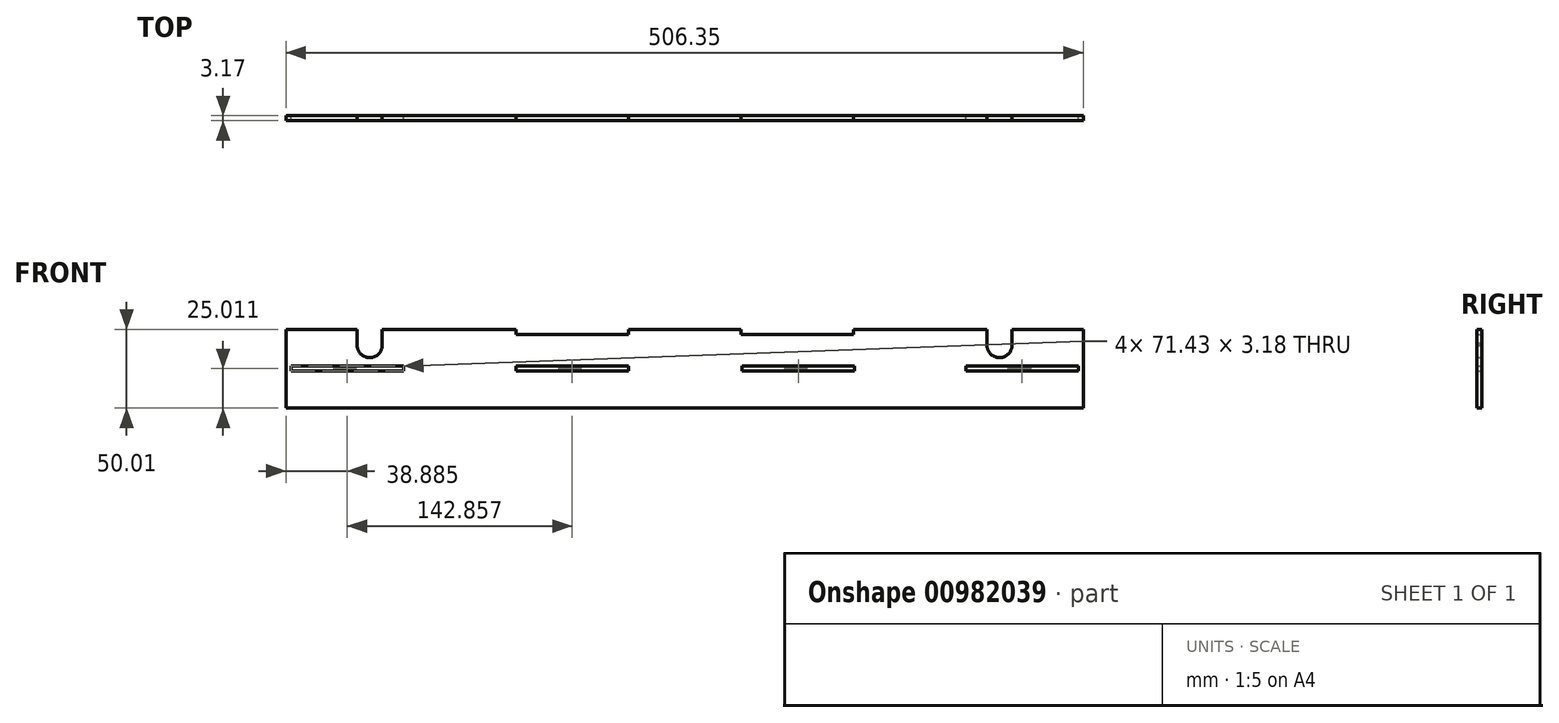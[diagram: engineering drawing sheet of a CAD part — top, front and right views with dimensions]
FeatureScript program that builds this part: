
annotation { "Feature Type Name" : "Feature", "Feature Type Description" : "" }
export const myFeature = defineFeature(function(context is Context, id is Id, definition is map)
    precondition{}
    {
        {
            var Q0;
            Q0=qCreatedBy(makeId("Front.planeOp"),FACE);
            var sketch = newSketch(context, id + "F0", { "sketchPlane" : qUnion([Q0])});
            skLineSegment(sketch, "E0.left", {"start": v(161.22, -50.9) * mm, "end": v(161.22, -0.9) * mm});
            skLineSegment(sketch, "E0.right", {"start": v(-338.78, -50.9) * mm, "end": v(-338.78, -0.9) * mm});
            skCircle(sketch, "E1", {"center": v(-288.78, -10.9) * mm, "radius": 8 * mm});
            skLineSegment(sketch, "E2", {"start": v(-88.78, -0.9) * mm, "end": v(-88.78, -50.9) * mm, "construction": true});
            skLineSegment(sketch, "E3.left", {"start": v(-338.78, -27.5) * mm, "end": v(-338.78, -24.32) * mm});
            skLineSegment(sketch, "E4", {"start": v(-338.78, -50.9) * mm, "end": v(161.22, -50.9) * mm});
            skCircle(sketch, "E5.MirrorC", {"center": v(111.22, -10.9) * mm, "radius": 8 * mm});
            skLineSegment(sketch, "E6.top", {"start": v(-296.77, -0.9) * mm, "end": v(-280.87, -0.9) * mm});
            skLineSegment(sketch, "E6.left", {"start": v(-296.77, -11.3) * mm, "end": v(-296.77, -0.9) * mm});
            skLineSegment(sketch, "E6.right", {"start": v(-280.87, -11.3) * mm, "end": v(-280.87, -0.9) * mm});
            skLineSegment(sketch, "E7", {"start": v(-296.77, -11.3) * mm, "end": v(-280.87, -11.3) * mm});
            skLineSegment(sketch, "E8.bottom", {"start": v(103.22, -11.1) * mm, "end": v(119.26, -11.1) * mm});
            skLineSegment(sketch, "E8.top", {"start": v(103.22, -0.9) * mm, "end": v(119.26, -0.9) * mm});
            skLineSegment(sketch, "E8.left", {"start": v(103.22, -11.1) * mm, "end": v(103.22, -0.9) * mm});
            skLineSegment(sketch, "E8.right", {"start": v(119.26, -11.1) * mm, "end": v(119.26, -0.9) * mm});
            skLineSegment(sketch, "E9.bottom", {"start": v(161.22, -24.32) * mm, "end": v(-338.78, -24.32) * mm, "construction": true});
            skLineSegment(sketch, "E10.top", {"start": v(-338.78, -27.5) * mm, "end": v(-267.35, -27.5) * mm});
            skLineSegment(sketch, "E10.left", {"start": v(-338.78, -24.32) * mm, "end": v(-338.78, -27.5) * mm});
            skLineSegment(sketch, "E10.right", {"start": v(-267.35, -24.32) * mm, "end": v(-267.35, -27.5) * mm});
            skLineSegment(sketch, "E11.1.0.0", {"start": v(-195.92, -27.5) * mm, "end": v(-124.5, -27.5) * mm});
            skLineSegment(sketch, "E11.1.0.2", {"start": v(-195.92, -24.32) * mm, "end": v(-195.92, -27.5) * mm});
            skLineSegment(sketch, "E11.1.0.3", {"start": v(-124.5, -24.32) * mm, "end": v(-124.5, -27.5) * mm});
            skLineSegment(sketch, "E11.1.0.4", {"start": v(-124.5, -24.32) * mm, "end": v(-124.5, -27.5) * mm});
            skLineSegment(sketch, "E11.2.0.0", {"start": v(-52.25, -27.5) * mm, "end": v(19.18, -27.5) * mm});
            skLineSegment(sketch, "E11.2.0.2", {"start": v(-52.25, -24.32) * mm, "end": v(-52.25, -27.5) * mm});
            skLineSegment(sketch, "E11.2.0.3", {"start": v(19.18, -24.32) * mm, "end": v(19.18, -27.5) * mm});
            skLineSegment(sketch, "E11.2.0.4", {"start": v(19.18, -24.32) * mm, "end": v(19.18, -27.5) * mm});
            skLineSegment(sketch, "E11.3.0.0", {"start": v(89.8, -27.5) * mm, "end": v(161.22, -27.5) * mm});
            skLineSegment(sketch, "E11.3.0.2", {"start": v(89.8, -24.32) * mm, "end": v(89.8, -27.5) * mm});
            skLineSegment(sketch, "E11.3.0.3", {"start": v(161.22, -24.32) * mm, "end": v(161.22, -27.5) * mm});
            skLineSegment(sketch, "E11.3.0.4", {"start": v(161.22, -24.32) * mm, "end": v(161.22, -27.5) * mm});
            skLineSegment(sketch, "E11.direction1", {"start": v(-338.78, -27.5) * mm, "end": v(-195.92, -27.5) * mm, "construction": true});
            skLineSegment(sketch, "E12", {"start": v(89.8, -24.32) * mm, "end": v(161.22, -24.32) * mm});
            skLineSegment(sketch, "E13", {"start": v(19.18, -24.32) * mm, "end": v(-52.25, -24.32) * mm});
            skLineSegment(sketch, "E14", {"start": v(-124.5, -24.32) * mm, "end": v(-195.92, -24.32) * mm});
            skLineSegment(sketch, "E15", {"start": v(-267.35, -24.32) * mm, "end": v(-338.78, -24.32) * mm});
            skLineSegment(sketch, "E16.bottom", {"start": v(-338.78, -0.9) * mm, "end": v(-341.95, -0.9) * mm});
            skLineSegment(sketch, "E16.left", {"start": v(-338.78, -0.9) * mm, "end": v(-338.78, -50.9) * mm});
            skLineSegment(sketch, "E16.right", {"start": v(-341.95, -0.9) * mm, "end": v(-341.95, -50.9) * mm});
            skLineSegment(sketch, "E17", {"start": v(-338.78, -50.9) * mm, "end": v(-341.95, -50.9) * mm});
            skLineSegment(sketch, "E18.bottom", {"start": v(161.22, -0.9) * mm, "end": v(164.4, -0.9) * mm});
            skLineSegment(sketch, "E18.left", {"start": v(161.22, -0.9) * mm, "end": v(161.22, -50.92) * mm});
            skLineSegment(sketch, "E18.right", {"start": v(164.4, -0.9) * mm, "end": v(164.4, -50.92) * mm});
            skLineSegment(sketch, "E19", {"start": v(161.22, -50.9) * mm, "end": v(164.4, -50.92) * mm});
            skLineSegment(sketch, "E20.bottom", {"start": v(161.22, -0.9) * mm, "end": v(-338.78, -0.9) * mm, "construction": true});
            skLineSegment(sketch, "E21.left", {"start": v(-338.78, -0.9) * mm, "end": v(-338.78, -4.08) * mm});
            skLineSegment(sketch, "E22.bottom", {"start": v(-267.35, -0.9) * mm, "end": v(-195.92, -0.9) * mm});
            skLineSegment(sketch, "E23.1.0.0", {"start": v(-195.92, -4.08) * mm, "end": v(-124.5, -4.08) * mm});
            skLineSegment(sketch, "E23.1.0.1", {"start": v(-124.5, -0.9) * mm, "end": v(-53.06, -0.9) * mm});
            skLineSegment(sketch, "E23.1.0.2", {"start": v(-195.92, -0.9) * mm, "end": v(-195.92, -4.08) * mm});
            skLineSegment(sketch, "E23.1.0.3", {"start": v(-124.5, -0.9) * mm, "end": v(-124.5, -4.08) * mm});
            skLineSegment(sketch, "E23.1.0.4", {"start": v(-124.5, -0.9) * mm, "end": v(-124.5, -4.08) * mm});
            skLineSegment(sketch, "E23.2.0.0", {"start": v(-53.06, -4.08) * mm, "end": v(18.36, -4.08) * mm});
            skLineSegment(sketch, "E23.2.0.1", {"start": v(18.36, -0.9) * mm, "end": v(89.8, -0.9) * mm});
            skLineSegment(sketch, "E23.2.0.2", {"start": v(-53.06, -0.9) * mm, "end": v(-53.06, -4.08) * mm});
            skLineSegment(sketch, "E23.2.0.3", {"start": v(18.36, -0.9) * mm, "end": v(18.36, -4.08) * mm});
            skLineSegment(sketch, "E23.2.0.4", {"start": v(18.36, -0.9) * mm, "end": v(18.36, -4.08) * mm});
            skLineSegment(sketch, "E23.3.0.3", {"start": v(161.22, -0.9) * mm, "end": v(161.22, -4.08) * mm});
            skLineSegment(sketch, "E23.3.0.4", {"start": v(161.22, -0.9) * mm, "end": v(161.22, -4.08) * mm});
            skLineSegment(sketch, "E23.direction1", {"start": v(-338.78, -4.08) * mm, "end": v(-195.92, -4.08) * mm, "construction": true});
            skLineSegment(sketch, "E24", {"start": v(-338.78, -0.9) * mm, "end": v(-267.35, -0.9) * mm});
            skLineSegment(sketch, "E25", {"start": v(89.8, -0.9) * mm, "end": v(161.22, -0.9) * mm});
            skSolve(sketch);
        }
        {
            var Q0;
            Q0=makeQuery(id+"F0.imprint","IMPRINT",FACE,{"disambiguationData":[TD([[makeQuery(id+"F0.imprint","IMPRINT",EDGE,{"derivedFrom":sQuery(id+"F0.wireOp",EDGE,"E16.bottom")}),1.0]])]});
            var Q1;
            Q1=makeQuery(id+"F0.imprint","IMPRINT",FACE,{"disambiguationData":[TD([[makeQuery(id+"F0.imprint","IMPRINT",EDGE,{"derivedFrom":sQuery(id+"F0.wireOp",EDGE,"E18.bottom")}),-1.0]])]});
            var Q2;
            {var subQ15=sQuery(id+"F0.wireOp",EDGE,"E0.right");Q2=makeQuery(id+"F0.imprint","IMPRINT",FACE,{"disambiguationData":[TD([[makeQuery(id+"F0.imprint","IMPRINT",EDGE,{"derivedFrom":subQ15}),-1.0]])]});}
            extrude(context, id + "F1", {"entities" : qUnion([Q0, Q1, Q2]), "flatOperationType" : FlatOperationType.REMOVE, "depth" : 3.17 * mm, "offsetDistance" : 25.4 * mm, "domain" : OperationDomain.MODEL});
        }
    });
